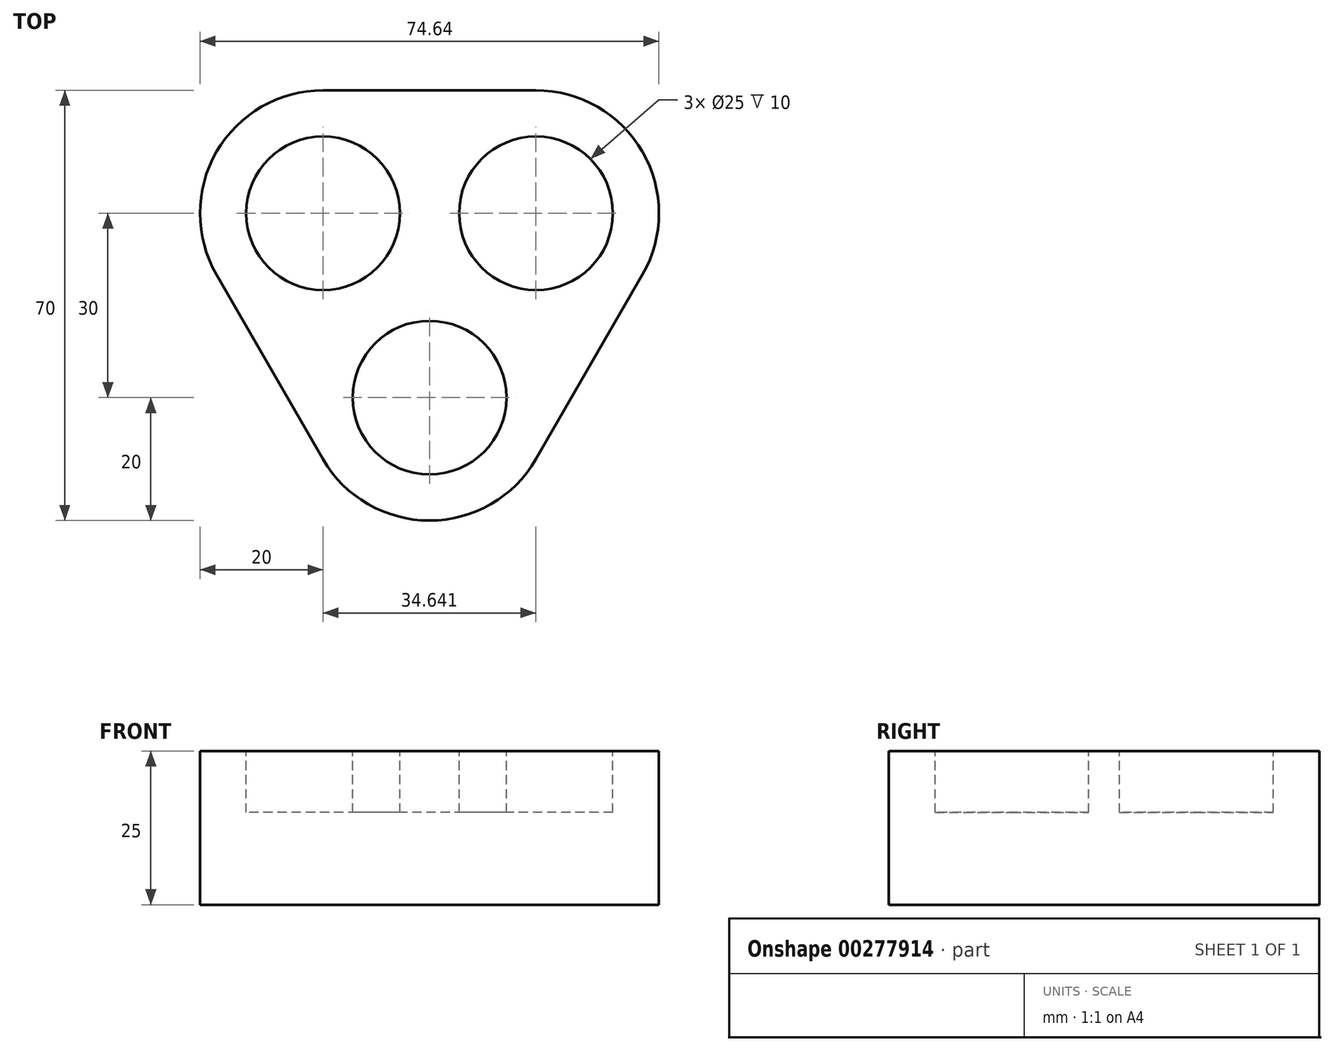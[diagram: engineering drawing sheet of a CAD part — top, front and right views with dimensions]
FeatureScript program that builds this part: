
annotation { "Feature Type Name" : "Feature", "Feature Type Description" : "" }
export const myFeature = defineFeature(function(context is Context, id is Id, definition is map)
    precondition{}
    {
        {
            var Q0;
            Q0=qCreatedBy(makeId("Top.planeOp"),FACE);
            var sketch = newSketch(context, id + "F0", { "sketchPlane" : qUnion([Q0])});
            skCircle(sketch, "E0.cCircle", {"center": v(0, 0) * mm, "radius": 30 * mm, "construction": true});
            skLineSegment(sketch, "E0.0", {"start": v(-17.32, 30) * mm, "end": v(17.32, 30) * mm});
            skLineSegment(sketch, "E0.1", {"start": v(34.64, 0) * mm, "end": v(17.32, -30) * mm});
            skLineSegment(sketch, "E0.2", {"start": v(-17.32, -30) * mm, "end": v(-34.64, 0) * mm});
            skPoint(sketch, "E0.0.midPoint", {"position": v(0, 30) * mm});
            skLineSegment(sketch, "E1", {"start": v(0, 0) * mm, "end": v(-51.96, 30) * mm, "construction": true});
            skCircle(sketch, "E2", {"center": v(-17.32, 10) * mm, "radius": 12.5 * mm, "construction": true});
            skCircle(sketch, "E3.1.0", {"center": v(0, -20) * mm, "radius": 12.5 * mm, "construction": true});
            skCircle(sketch, "E3.2.0", {"center": v(17.32, 10) * mm, "radius": 12.5 * mm, "construction": true});
            skLineSegment(sketch, "E4", {"start": v(-17.32, 10) * mm, "end": v(-17.32, 30) * mm, "construction": true});
            skPoint(sketch, "E5.visualSharp", {"position": v(-51.96, 30) * mm});
            skArc(sketch, "E5.filletArc", {"start": v(-17.32, 30) * mm, "mid": v(-34.64, 20) * mm, "end": v(-34.64, 0) * mm});
            skPoint(sketch, "E6.visualSharp", {"position": v(0, -60) * mm});
            skArc(sketch, "E6.filletArc", {"start": v(-17.32, -30) * mm, "mid": v(0, -40) * mm, "end": v(17.32, -30) * mm});
            skPoint(sketch, "E7.visualSharp", {"position": v(51.96, 30) * mm});
            skArc(sketch, "E7.filletArc", {"start": v(34.64, 0) * mm, "mid": v(34.64, 20) * mm, "end": v(17.32, 30) * mm});
            skSolve(sketch);
        }
        {
            var Q0;
            Q0=qSketchRegion(id+"F0",true);
            extrude(context, id + "F1", {"entities" : qUnion([Q0]), "depth" : 25 * mm});
        }
        {
            var Q0;
            Q0=makeQuery(id+"F1.opExtrude","CAP_FACE",FACE,{"disambiguationData":[OSD([sQuery(id+"F0.wireOp",EDGE,"E0.0"),sQuery(id+"F0.wireOp",EDGE,"E0.1"),sQuery(id+"F0.wireOp",EDGE,"E0.2"),sQuery(id+"F0.wireOp",EDGE,"E5.filletArc"),sQuery(id+"F0.wireOp",EDGE,"E6.filletArc"),sQuery(id+"F0.wireOp",EDGE,"E7.filletArc")])],"isStart":false});
            var sketch = newSketch(context, id + "F2", { "sketchPlane" : qUnion([Q0])});
            skLineSegment(sketch, "E8", {"start": v(0, 0) * mm, "end": v(-34.64, 20) * mm, "construction": true});
            skCircle(sketch, "E9", {"center": v(-17.32, 10) * mm, "radius": 12.5 * mm});
            skCircle(sketch, "E10.1.0", {"center": v(0, -20) * mm, "radius": 12.5 * mm});
            skCircle(sketch, "E10.2.0", {"center": v(17.32, 10) * mm, "radius": 12.5 * mm});
            skPoint(sketch, "E10.center", {"position": v(0, 0) * mm});
            skSolve(sketch);
        }
        {
            var Q0;
            Q0=qSketchRegion(id+"F2",true);
            extrude(context, id + "F3", {"entities" : qUnion([Q0]), "operationType" : NewBodyOperationType.REMOVE, "oppositeDirection" : true, "depth" : 10 * mm});
        }
    });
